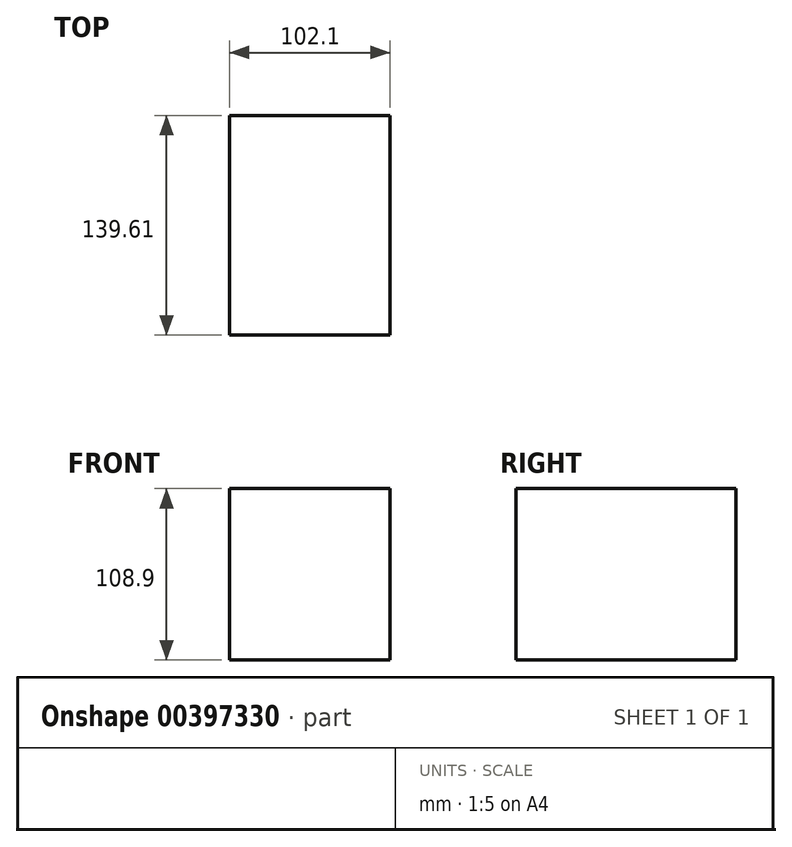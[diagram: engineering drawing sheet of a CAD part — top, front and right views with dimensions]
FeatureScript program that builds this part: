
annotation { "Feature Type Name" : "Feature", "Feature Type Description" : "" }
export const myFeature = defineFeature(function(context is Context, id is Id, definition is map)
    precondition{}
    {
        {
            var Q0;
            Q0=qCreatedBy(makeId("Right.planeOp"),FACE);
            var sketch = newSketch(context, id + "F0", { "sketchPlane" : qUnion([Q0])});
            skLineSegment(sketch, "E0.bottom", {"start": v(-66.46, 57.12) * mm, "end": v(73.15, 57.12) * mm});
            skLineSegment(sketch, "E0.top", {"start": v(-66.46, -51.78) * mm, "end": v(73.15, -51.78) * mm});
            skLineSegment(sketch, "E0.left", {"start": v(-66.46, 57.12) * mm, "end": v(-66.46, -51.78) * mm});
            skLineSegment(sketch, "E0.right", {"start": v(73.15, 57.12) * mm, "end": v(73.15, -51.78) * mm});
            skSolve(sketch);
        }
        {
            var Q0;
            Q0=makeQuery(id+"F0.imprint","IMPRINT",FACE,{"disambiguationData":[TD([[makeQuery(id+"F0.imprint","IMPRINT",EDGE,{"derivedFrom":sQuery(id+"F0.wireOp",EDGE,"E0.bottom")}),-1.0]])]});
            extrude(context, id + "F1", {"entities" : qUnion([Q0]), "endBound" : BoundingType.SYMMETRIC, "depth" : 102.1 * mm});
        }
    });
